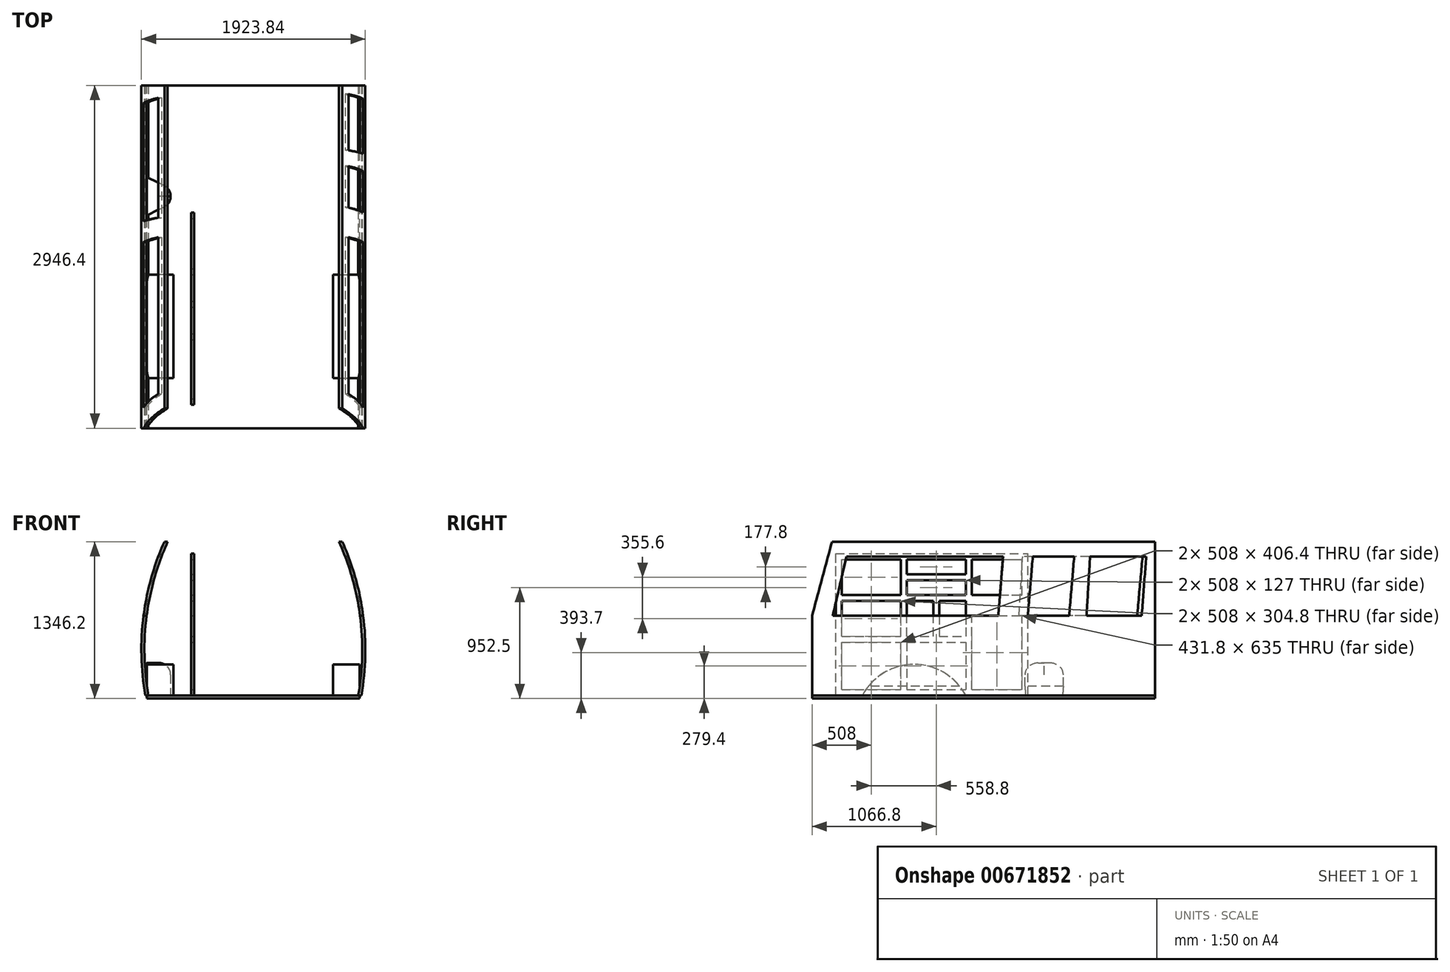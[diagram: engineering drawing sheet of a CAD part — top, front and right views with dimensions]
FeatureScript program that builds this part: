
annotation { "Feature Type Name" : "Feature", "Feature Type Description" : "" }
export const myFeature = defineFeature(function(context is Context, id is Id, definition is map)
    precondition{}
    {
        {
            var Q0;
            Q0=qCreatedBy(makeId("Top.planeOp"),FACE);
            var sketch = newSketch(context, id + "F0", { "sketchPlane" : qUnion([Q0])});
            skLineSegment(sketch, "E0.bottom", {"start": v(-914.4, 0) * mm, "end": v(914.4, 0) * mm});
            skLineSegment(sketch, "E0.top", {"start": v(-914.4, 2946.4) * mm, "end": v(914.4, 2946.4) * mm});
            skLineSegment(sketch, "E0.left", {"start": v(-914.4, 0) * mm, "end": v(-914.4, 2946.4) * mm});
            skLineSegment(sketch, "E0.right", {"start": v(914.4, 0) * mm, "end": v(914.4, 2946.4) * mm});
            skSolve(sketch);
        }
        {
            var Q0;
            Q0=makeQuery(id+"F0.imprint","IMPRINT",FACE,{"disambiguationData":[TD([[makeQuery(id+"F0.imprint","IMPRINT",EDGE,{"derivedFrom":sQuery(id+"F0.wireOp",EDGE,"E0.bottom")}),1.0]])]});
            extrude(context, id + "F1", {"entities" : qUnion([Q0]), "oppositeDirection" : true, "depth" : 25.4 * mm, "offsetDistance" : 25.4 * mm});
        }
        {
            var Q0;
            Q0=makeQuery(id+"F1.opExtrude","SWEPT_FACE",FACE,{"disambiguationData":[OSD([sQuery(id+"F0.wireOp",EDGE,"E0.left")])]});
            var sketch = newSketch(context, id + "F2", { "sketchPlane" : qUnion([Q0])});
            skArc(sketch, "E1", {"start": v(-431.8, 0) * mm, "mid": v(-876.3, 266.7) * mm, "end": v(-1320.8, 0) * mm});
            skPoint(sketch, "E2", {"position": v(-876.3, 266.7) * mm});
            skLineSegment(sketch, "E3", {"start": v(-431.8, 0) * mm, "end": v(-1320.8, 0) * mm});
            skSolve(sketch);
        }
        {
            var Q0;
            Q0=makeQuery(id+"F2.imprint","IMPRINT",FACE,{"disambiguationData":[TD([[makeQuery(id+"F2.imprint","IMPRINT",EDGE,{"derivedFrom":sQuery(id+"F2.wireOp",EDGE,"E1")}),1.0]])]});
            extrude(context, id + "F3", {"entities" : qUnion([Q0]), "operationType" : NewBodyOperationType.ADD, "oppositeDirection" : true, "depth" : 228.6 * mm, "offsetDistance" : 25.4 * mm});
        }
        {
            var Q0;
            Q0=makeQuery(id+"F1.opExtrude","SWEPT_BODY",BODY,{"disambiguationData":[OSD([sQuery(id+"F0.wireOp",EDGE,"E0.bottom"),sQuery(id+"F0.wireOp",EDGE,"E0.top"),sQuery(id+"F0.wireOp",EDGE,"E0.left"),sQuery(id+"F0.wireOp",EDGE,"E0.right")])]});
            var Q1;
            Q1=qCreatedBy(makeId("Right.planeOp"),FACE);
            mirror(context, id + "F4", {"operationType" : NewBodyOperationType.ADD, "entities" : qUnion([Q0]), "mirrorPlane" : qUnion([Q1])});
        }
        {
            var Q0;
            Q0=makeQuery(id+"F3.boolean.opBoolean","MERGE",FACE,{"derivedFrom":[makeQuery(id+"F1.opExtrude","SWEPT_FACE",FACE,{"disambiguationData":[OSD([sQuery(id+"F0.wireOp",EDGE,"E0.left")])]}),makeQuery(id+"F3.opExtrude","CAP_FACE",FACE,{"disambiguationData":[OSD([sQuery(id+"F2.wireOp",EDGE,"E1"),sQuery(id+"F2.wireOp",EDGE,"E3")])],"isStart":true})]});
            var sketch = newSketch(context, id + "F5", { "sketchPlane" : qUnion([Q0])});
            skLineSegment(sketch, "E4.bottom", {"start": v(-2159, 0) * mm, "end": v(-1828.8, 0) * mm});
            skLineSegment(sketch, "E4.top", {"start": v(-2159, 279.4) * mm, "end": v(-1828.8, 279.4) * mm});
            skLineSegment(sketch, "E4.left", {"start": v(-2159, 0) * mm, "end": v(-2159, 279.4) * mm});
            skLineSegment(sketch, "E4.right", {"start": v(-1828.8, 0) * mm, "end": v(-1828.8, 279.4) * mm});
            skSolve(sketch);
        }
        {
            var Q0;
            Q0 = qSketchRegion(id + "F5", true);
            extrude(context, id + "F6", {"entities" : qUnion([Q0]), "operationType" : NewBodyOperationType.ADD, "oppositeDirection" : true, "depth" : 203.2 * mm, "offsetDistance" : 25.4 * mm});
        }
        {
            var Q0;
            Q0=qCreatedBy(makeId("Front.planeOp"),FACE);
            var sketch = newSketch(context, id + "F7", { "sketchPlane" : qUnion([Q0])});
            skArc(sketch, "E5", {"start": v(-736.6, 1320.8) * mm, "mid": v(-919.16, 672.9) * mm, "end": v(-901.7, 0) * mm});
            skArc(sketch, "E6.0", {"start": v(-764.45, 1320.8) * mm, "mid": v(-944.8, 672.6) * mm, "end": v(-927.5, 0) * mm});
            skLineSegment(sketch, "E7", {"start": v(-736.6, 1320.8) * mm, "end": v(-764.45, 1320.8) * mm});
            skLineSegment(sketch, "E8", {"start": v(-901.7, 0) * mm, "end": v(-927.5, 0) * mm});
            skLineSegment(sketch, "E9", {"start": v(0, 0) * mm, "end": v(0, 1318.84) * mm, "construction": true});
            skLineSegment(sketch, "E10.MirrorCS", {"start": v(901.7, 0) * mm, "end": v(927.5, 0) * mm});
            skLineSegment(sketch, "E11.MirrorCS", {"start": v(736.6, 1320.8) * mm, "end": v(764.45, 1320.8) * mm});
            skArc(sketch, "E12.MirrorCS", {"start": v(764.45, 1320.8) * mm, "mid": v(944.8, 672.6) * mm, "end": v(927.5, 0) * mm});
            skArc(sketch, "E13.MirrorCS", {"start": v(736.6, 1320.8) * mm, "mid": v(919.16, 672.9) * mm, "end": v(901.7, 0) * mm});
            skLineSegment(sketch, "E14", {"start": v(-901.7, 0) * mm, "end": v(-780.75, -679.15) * mm, "construction": true});
            skSolve(sketch);
        }
        {
            var Q0;
            Q0 = qSketchRegion(id + "F7", true);
            extrude(context, id + "F8", {"entities" : qUnion([Q0]), "operationType" : NewBodyOperationType.ADD, "oppositeDirection" : true, "depth" : 2946.4 * mm, "offsetDistance" : 25.4 * mm});
        }
        {
            var Q0;
            Q0=makeQuery(id+"F6.opExtrude","CAP_EDGE",EDGE,{"disambiguationData":[OSD([sQuery(id+"F5.wireOp",EDGE,"E4.left")])],"isStart":false});
            chamfer(context, id + "F9", {"entities" : qUnion([Q0]), "chamferType" : ChamferType.TWO_OFFSETS, "width1" : 101.6 * mm, "oppositeDirection" : false, "width2" : 203.2 * mm, "tangentPropagation" : true});
        }
        {
            var Q0;
            Q0=makeQuery(id+"F6.opExtrude","CAP_EDGE",EDGE,{"disambiguationData":[OSD([sQuery(id+"F5.wireOp",EDGE,"E4.right")])],"isStart":false});
            chamfer(context, id + "F10", {"entities" : qUnion([Q0]), "chamferType" : ChamferType.TWO_OFFSETS, "width1" : 203.2 * mm, "oppositeDirection" : false, "width2" : 101.6 * mm, "tangentPropagation" : true});
        }
        {
            var Q0;
            Q0=makeQuery(id+"F6.opExtrude","CAP_EDGE",EDGE,{"disambiguationData":[OSD([sQuery(id+"F5.wireOp",EDGE,"E4.top")])],"isStart":false});
            fillet(context, id + "F11", {"entities" : qUnion([Q0]), "radius" : 101.6 * mm, "tangentPropagation" : true, "allowEdgeOverflow" : false});
        }
        {
            var Q0;
            Q0=makeQuery(id+"F9.opChamfer","BLEND_EDGE",EDGE,{"blendedFrom":[makeQuery(id+"F6.opExtrude","CAP_EDGE",EDGE,{"disambiguationData":[OSD([sQuery(id+"F5.wireOp",EDGE,"E4.left")])],"isStart":false}),makeQuery(id+"F6.opExtrude","SWEPT_FACE",FACE,{"disambiguationData":[OSD([sQuery(id+"F5.wireOp",EDGE,"E4.top")])]})],"blendedInto":[makeQuery(id+"F6.opExtrude","SWEPT_FACE",FACE,{"disambiguationData":[OSD([sQuery(id+"F5.wireOp",EDGE,"E4.top")])]})]});
            var Q1;
            Q1=makeQuery(id+"F11.opFillet","BLEND_EDGE",EDGE,{"blendedFrom":[makeQuery(id+"F6.opExtrude","CAP_EDGE",EDGE,{"disambiguationData":[OSD([sQuery(id+"F5.wireOp",EDGE,"E4.top")])],"isStart":false}),makeQuery(id+"F10.opChamfer","BLEND_FACE",FACE,{"disambiguationData":[OSD([sQuery(id+"F5.wireOp",EDGE,"E4.right")])]})],"blendedInto":[makeQuery(id+"F10.opChamfer","BLEND_FACE",FACE,{"disambiguationData":[OSD([sQuery(id+"F5.wireOp",EDGE,"E4.right")])]})]});
            fillet(context, id + "F12", {"entities" : qUnion([Q0, Q1]), "radius" : 101.6 * mm, "tangentPropagation" : true, "allowEdgeOverflow" : false});
        }
        {
            var Q0;
            Q0=qCreatedBy(makeId("Right.planeOp"),FACE);
            var sketch = newSketch(context, id + "F13", { "sketchPlane" : qUnion([Q0])});
            skLineSegment(sketch, "E15", {"start": v(0, 0) * mm, "end": v(0, 685.8) * mm, "construction": true});
            skLineSegment(sketch, "E16", {"start": v(0, 685.8) * mm, "end": v(177.8, 1346.2) * mm});
            skLineSegment(sketch, "E17", {"start": v(177.8, 1346.2) * mm, "end": v(0, 1346.2) * mm});
            skLineSegment(sketch, "E18", {"start": v(0, 1346.2) * mm, "end": v(0, 685.8) * mm, "construction": true});
            skLineSegment(sketch, "E19", {"start": v(0, 1346.2) * mm, "end": v(-90.24, 1346.2) * mm});
            skLineSegment(sketch, "E20", {"start": v(-90.24, 1346.2) * mm, "end": v(-90.24, 350.64) * mm});
            skLineSegment(sketch, "E21", {"start": v(-90.24, 350.64) * mm, "end": v(0, 685.8) * mm});
            skSolve(sketch);
        }
        {
            var Q0;
            Q0 = qSketchRegion(id + "F13", true);
            extrude(context, id + "F14", {"entities" : qUnion([Q0]), "operationType" : NewBodyOperationType.REMOVE, "endBound" : BoundingType.SYMMETRIC, "oppositeDirection" : true, "depth" : 1981.2 * mm, "offsetDistance" : 25.4 * mm});
        }
        {
            var Q0;
            Q0=qCreatedBy(makeId("Right.planeOp"),FACE);
            var sketch = newSketch(context, id + "F15", { "sketchPlane" : qUnion([Q0])});
            skLineSegment(sketch, "E22", {"start": v(177.8, 685.8) * mm, "end": v(295.1, 1193.8) * mm});
            skLineSegment(sketch, "E23.0", {"start": v(0, 1193.8) * mm, "end": v(2941.3, 1193.8) * mm, "construction": true});
            skLineSegment(sketch, "E23.1", {"start": v(0, 685.8) * mm, "end": v(2946.4, 685.8) * mm, "construction": true});
            skLineSegment(sketch, "E24", {"start": v(177.8, 685.8) * mm, "end": v(1600.2, 685.8) * mm});
            skLineSegment(sketch, "E25", {"start": v(1600.2, 685.8) * mm, "end": v(1641.3, 1193.8) * mm});
            skLineSegment(sketch, "E26", {"start": v(1641.3, 1193.8) * mm, "end": v(295.1, 1193.8) * mm});
            skLineSegment(sketch, "E27", {"start": v(1778, 685.8) * mm, "end": v(1810.24, 1193.8) * mm});
            skLineSegment(sketch, "E28", {"start": v(1810.24, 1193.8) * mm, "end": v(2839.7, 1193.8) * mm});
            skLineSegment(sketch, "E29", {"start": v(2839.7, 1193.8) * mm, "end": v(2794, 685.8) * mm});
            skLineSegment(sketch, "E30", {"start": v(2794, 685.8) * mm, "end": v(1778, 685.8) * mm});
            skSolve(sketch);
        }
        {
            var Q0;
            Q0 = qSketchRegion(id + "F15", true);
            extrude(context, id + "F16", {"entities" : qUnion([Q0]), "operationType" : NewBodyOperationType.REMOVE, "endBound" : BoundingType.THROUGH_ALL, "oppositeDirection" : true, "depth" : 25.4 * mm, "offsetDistance" : 25.4 * mm});
        }
        {
            var Q0;
            Q0=qCreatedBy(makeId("Right.planeOp"),FACE);
            var sketch = newSketch(context, id + "F17", { "sketchPlane" : qUnion([Q0])});
            skLineSegment(sketch, "E31.0", {"start": v(0, 1193.8) * mm, "end": v(2941.3, 1193.8) * mm, "construction": true});
            skLineSegment(sketch, "E31.1", {"start": v(0, 685.8) * mm, "end": v(2946.4, 685.8) * mm, "construction": true});
            skLineSegment(sketch, "E32.0", {"start": v(177.8, 685.8) * mm, "end": v(295.1, 1193.8) * mm});
            skLineSegment(sketch, "E32.1", {"start": v(1600.2, 685.8) * mm, "end": v(1641.3, 1193.8) * mm});
            skLineSegment(sketch, "E32.2", {"start": v(177.8, 685.8) * mm, "end": v(1600.2, 685.8) * mm});
            skLineSegment(sketch, "E33.0", {"start": v(1641.3, 1193.8) * mm, "end": v(295.1, 1193.8) * mm});
            skLineSegment(sketch, "E34", {"start": v(1853.72, 685.8) * mm, "end": v(1896.66, 1193.8) * mm});
            skLineSegment(sketch, "E35", {"start": v(1896.66, 1193.8) * mm, "end": v(2252.26, 1193.8) * mm});
            skLineSegment(sketch, "E36", {"start": v(2252.26, 1193.8) * mm, "end": v(2209.32, 685.8) * mm});
            skLineSegment(sketch, "E37", {"start": v(2209.32, 685.8) * mm, "end": v(1853.72, 685.8) * mm});
            skLineSegment(sketch, "E38", {"start": v(2388.7, 1193.8) * mm, "end": v(2871.3, 1193.8) * mm});
            skLineSegment(sketch, "E39", {"start": v(2871.3, 1193.8) * mm, "end": v(2832.35, 685.8) * mm});
            skLineSegment(sketch, "E40", {"start": v(2832.35, 685.8) * mm, "end": v(2358.35, 685.8) * mm});
            skLineSegment(sketch, "E41", {"start": v(2358.35, 685.8) * mm, "end": v(2388.7, 1193.8) * mm});
            skSolve(sketch);
        }
        {
            var Q0;
            Q0 = qSketchRegion(id + "F17", true);
            extrude(context, id + "F18", {"entities" : qUnion([Q0]), "operationType" : NewBodyOperationType.REMOVE, "endBound" : BoundingType.THROUGH_ALL, "depth" : 25.4 * mm, "offsetDistance" : 25.4 * mm});
        }
        {
            var Q0;
            {var subQ5=sQuery(id+"F0.wireOp",EDGE,"E0.left");var subQ6=sQuery(id+"F0.wireOp",EDGE,"E0.bottom");Q0=makeQuery(id+"F8.boolean.opBoolean","SPLIT",FACE,{"disambiguationData":[TD([makeQuery(id+"F1.opExtrude","SWEPT_FACE",FACE,{"disambiguationData":[OSD([subQ6])]})])],"derivedFrom":makeQuery(id+"F6.boolean.opBoolean","MERGE",FACE,{"derivedFrom":[makeQuery(id+"F3.boolean.opBoolean","MERGE",FACE,{"derivedFrom":[makeQuery(id+"F1.opExtrude","SWEPT_FACE",FACE,{"disambiguationData":[OSD([subQ5])]}),makeQuery(id+"F3.opExtrude","CAP_FACE",FACE,{"disambiguationData":[OSD([sQuery(id+"F2.wireOp",EDGE,"E1"),sQuery(id+"F2.wireOp",EDGE,"E3")])],"isStart":true})]}),makeQuery(id+"F6.opExtrude","CAP_FACE",FACE,{"disambiguationData":[OSD([sQuery(id+"F5.wireOp",EDGE,"E4.bottom"),sQuery(id+"F5.wireOp",EDGE,"E4.top"),sQuery(id+"F5.wireOp",EDGE,"E4.left"),sQuery(id+"F5.wireOp",EDGE,"E4.right")])],"isStart":true})]})});}
            cPlane(context, id + "F19", {"entities" : qUnion([Q0]), "cplaneType" : CPlaneType.OFFSET, "offset" : 406.4 * mm, "oppositeDirection" : true, "width" : 152.4 * mm, "height" : 152.4 * mm});
        }
        {
            var Q0;
            Q0=qCreatedBy(id+"F19.planeOp",FACE);
            var sketch = newSketch(context, id + "F20", { "sketchPlane" : qUnion([Q0])});
            skLineSegment(sketch, "E42.bottom", {"start": v(-203.2, 0) * mm, "end": v(-1854.2, 0) * mm});
            skLineSegment(sketch, "E42.top", {"start": v(-203.2, 1219.2) * mm, "end": v(-1854.2, 1219.2) * mm});
            skLineSegment(sketch, "E42.left", {"start": v(-203.2, 0) * mm, "end": v(-203.2, 1219.2) * mm});
            skLineSegment(sketch, "E42.right", {"start": v(-1854.2, 0) * mm, "end": v(-1854.2, 1219.2) * mm});
            skLineSegment(sketch, "E43.bottom", {"start": v(-254, 50.8) * mm, "end": v(-762, 50.8) * mm});
            skLineSegment(sketch, "E43.top", {"start": v(-254, 457.2) * mm, "end": v(-762, 457.2) * mm});
            skLineSegment(sketch, "E43.left", {"start": v(-254, 50.8) * mm, "end": v(-254, 457.2) * mm});
            skLineSegment(sketch, "E43.right", {"start": v(-762, 50.8) * mm, "end": v(-762, 457.2) * mm});
            skPoint(sketch, "E44", {"position": v(-1320.8, 0) * mm});
            skLineSegment(sketch, "E45.bottom", {"start": v(-1371.6, 50.8) * mm, "end": v(-1803.4, 50.8) * mm});
            skLineSegment(sketch, "E45.top", {"start": v(-1371.6, 685.8) * mm, "end": v(-1803.4, 685.8) * mm});
            skLineSegment(sketch, "E45.left", {"start": v(-1371.6, 50.8) * mm, "end": v(-1371.6, 685.8) * mm});
            skLineSegment(sketch, "E45.right", {"start": v(-1803.4, 50.8) * mm, "end": v(-1803.4, 685.8) * mm});
            skLineSegment(sketch, "E46.bottom", {"start": v(-254, 508) * mm, "end": v(-762, 508) * mm});
            skLineSegment(sketch, "E46.top", {"start": v(-254, 812.8) * mm, "end": v(-762, 812.8) * mm});
            skLineSegment(sketch, "E46.left", {"start": v(-254, 508) * mm, "end": v(-254, 812.8) * mm});
            skLineSegment(sketch, "E46.right", {"start": v(-762, 508) * mm, "end": v(-762, 812.8) * mm});
            skLineSegment(sketch, "E47.bottom", {"start": v(-254, 863.6) * mm, "end": v(-762, 863.6) * mm});
            skLineSegment(sketch, "E47.top", {"start": v(-254, 1168.4) * mm, "end": v(-762, 1168.4) * mm});
            skLineSegment(sketch, "E47.left", {"start": v(-254, 863.6) * mm, "end": v(-254, 1168.4) * mm});
            skLineSegment(sketch, "E47.right", {"start": v(-762, 863.6) * mm, "end": v(-762, 1168.4) * mm});
            skLineSegment(sketch, "E48.bottom", {"start": v(-812.8, 457.2) * mm, "end": v(-1320.8, 457.2) * mm});
            skLineSegment(sketch, "E48.top", {"start": v(-812.8, 50.8) * mm, "end": v(-1320.8, 50.8) * mm});
            skLineSegment(sketch, "E48.left", {"start": v(-812.8, 457.2) * mm, "end": v(-812.8, 50.8) * mm});
            skLineSegment(sketch, "E48.right", {"start": v(-1320.8, 457.2) * mm, "end": v(-1320.8, 50.8) * mm});
            skLineSegment(sketch, "E49.bottom", {"start": v(-812.8, 508) * mm, "end": v(-1041.4, 508) * mm});
            skLineSegment(sketch, "E49.top", {"start": v(-812.8, 812.8) * mm, "end": v(-1041.4, 812.8) * mm});
            skLineSegment(sketch, "E49.left", {"start": v(-812.8, 508) * mm, "end": v(-812.8, 812.8) * mm});
            skLineSegment(sketch, "E49.right", {"start": v(-1041.4, 508) * mm, "end": v(-1041.4, 812.8) * mm});
            skLineSegment(sketch, "E50.bottom", {"start": v(-1092.2, 812.8) * mm, "end": v(-1320.8, 812.8) * mm});
            skLineSegment(sketch, "E50.top", {"start": v(-1092.2, 508) * mm, "end": v(-1320.8, 508) * mm});
            skLineSegment(sketch, "E50.left", {"start": v(-1092.2, 812.8) * mm, "end": v(-1092.2, 508) * mm});
            skLineSegment(sketch, "E50.right", {"start": v(-1320.8, 812.8) * mm, "end": v(-1320.8, 508) * mm});
            skLineSegment(sketch, "E51.bottom", {"start": v(-812.8, 863.6) * mm, "end": v(-1320.8, 863.6) * mm});
            skLineSegment(sketch, "E51.top", {"start": v(-812.8, 990.6) * mm, "end": v(-1320.8, 990.6) * mm});
            skLineSegment(sketch, "E51.left", {"start": v(-812.8, 863.6) * mm, "end": v(-812.8, 990.6) * mm});
            skLineSegment(sketch, "E51.right", {"start": v(-1320.8, 863.6) * mm, "end": v(-1320.8, 990.6) * mm});
            skLineSegment(sketch, "E52.bottom", {"start": v(-1320.8, 1041.4) * mm, "end": v(-812.8, 1041.4) * mm});
            skLineSegment(sketch, "E52.top", {"start": v(-1320.8, 1168.4) * mm, "end": v(-812.8, 1168.4) * mm});
            skLineSegment(sketch, "E52.left", {"start": v(-1320.8, 1041.4) * mm, "end": v(-1320.8, 1168.4) * mm});
            skLineSegment(sketch, "E52.right", {"start": v(-812.8, 1041.4) * mm, "end": v(-812.8, 1168.4) * mm});
            skLineSegment(sketch, "E53.bottom", {"start": v(-1371.6, 863.6) * mm, "end": v(-1803.4, 863.6) * mm});
            skLineSegment(sketch, "E53.top", {"start": v(-1371.6, 1168.4) * mm, "end": v(-1803.4, 1168.4) * mm});
            skLineSegment(sketch, "E53.left", {"start": v(-1371.6, 863.6) * mm, "end": v(-1371.6, 1168.4) * mm});
            skLineSegment(sketch, "E53.right", {"start": v(-1803.4, 863.6) * mm, "end": v(-1803.4, 1168.4) * mm});
            skSolve(sketch);
        }
        {
            var Q0;
            Q0 = qSketchRegion(id + "F20", true);
            extrude(context, id + "F21", {"entities" : qUnion([Q0]), "depth" : 25.4 * mm, "offsetDistance" : 25.4 * mm});
        }
    });
